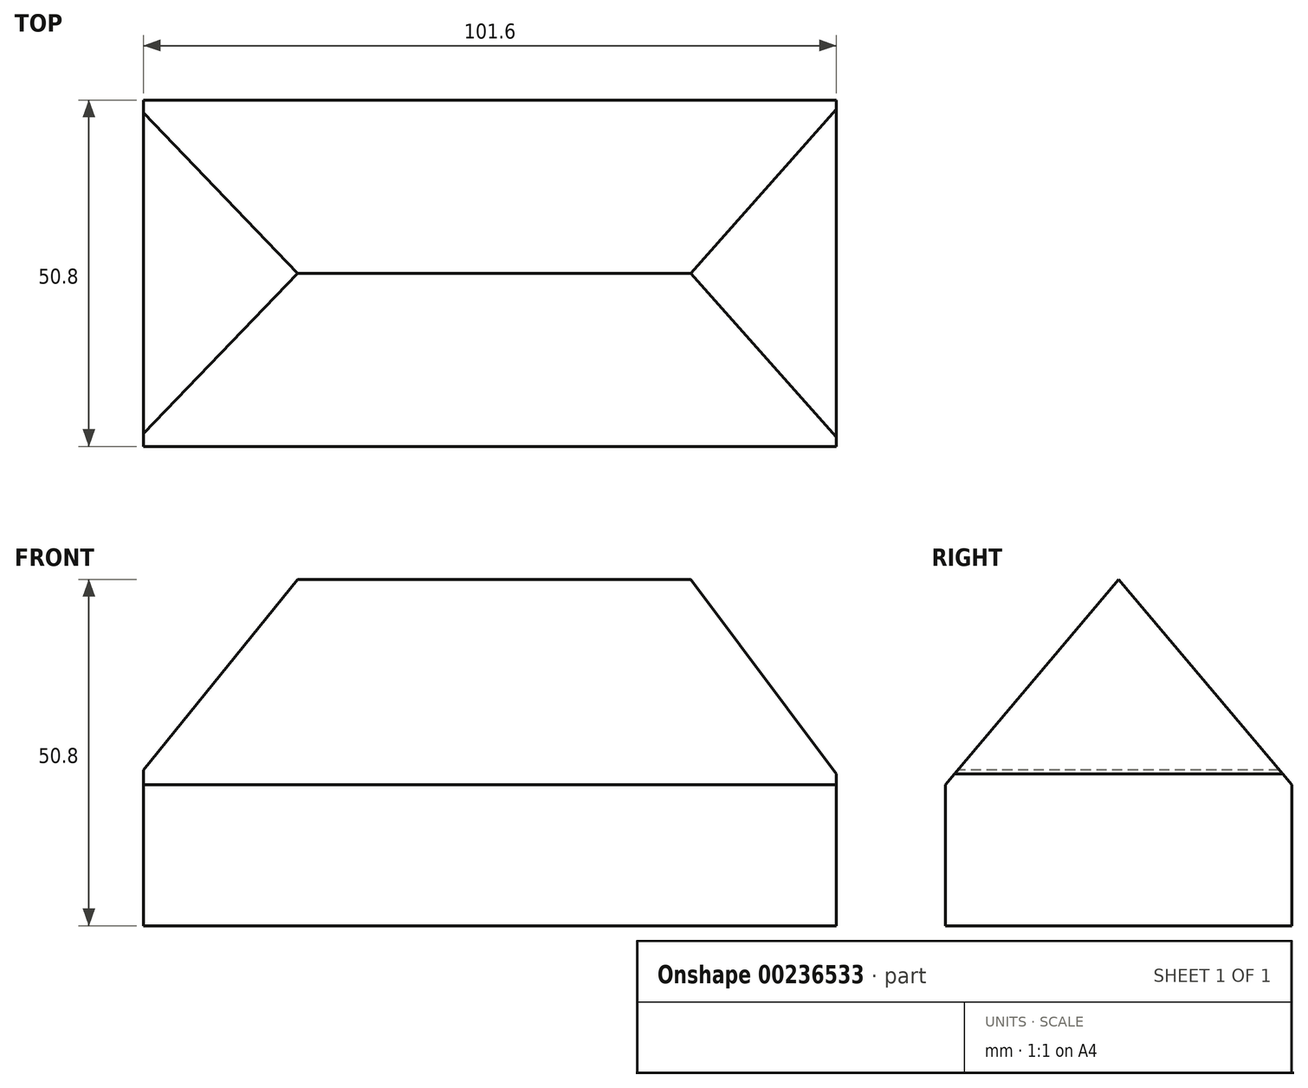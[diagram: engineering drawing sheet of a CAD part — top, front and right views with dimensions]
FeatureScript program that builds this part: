
annotation { "Feature Type Name" : "Feature", "Feature Type Description" : "" }
export const myFeature = defineFeature(function(context is Context, id is Id, definition is map)
    precondition{}
    {
        {
            var Q0;
            Q0=qCreatedBy(makeId("Top.planeOp"),FACE);
            var sketch = newSketch(context, id + "F0", { "sketchPlane" : qUnion([Q0])});
            skLineSegment(sketch, "E0.bottom", {"start": v(-44.73, 27.15) * mm, "end": v(56.87, 27.15) * mm});
            skLineSegment(sketch, "E0.top", {"start": v(-44.73, -23.65) * mm, "end": v(56.87, -23.65) * mm});
            skLineSegment(sketch, "E0.left", {"start": v(-44.73, 27.15) * mm, "end": v(-44.73, -23.65) * mm});
            skLineSegment(sketch, "E0.right", {"start": v(56.87, 27.15) * mm, "end": v(56.87, -23.65) * mm});
            skSolve(sketch);
        }
        {
            var Q0;
            Q0=makeQuery(id+"F0.imprint","IMPRINT",FACE,{"disambiguationData":[TD([[makeQuery(id+"F0.imprint","IMPRINT",EDGE,{"derivedFrom":sQuery(id+"F0.wireOp",EDGE,"E0.bottom")}),-1.0]])]});
            extrude(context, id + "F1", {"entities" : qUnion([Q0]), "depth" : 50.8 * mm});
        }
        {
            var Q0;
            Q0=makeQuery(id+"F1.opExtrude","SWEPT_FACE",FACE,{"disambiguationData":[OSD([sQuery(id+"F0.wireOp",EDGE,"E0.left")])]});
            var sketch = newSketch(context, id + "F2", { "sketchPlane" : qUnion([Q0])});
            skLineSegment(sketch, "E1", {"start": v(-1.75, 50.8) * mm, "end": v(23.65, 20.65) * mm});
            skLineSegment(sketch, "E2", {"start": v(23.65, 20.65) * mm, "end": v(23.65, 50.8) * mm});
            skLineSegment(sketch, "E3", {"start": v(23.65, 50.8) * mm, "end": v(-1.75, 50.8) * mm});
            skLineSegment(sketch, "E4", {"start": v(-27.15, 50.8) * mm, "end": v(-27.15, 20.65) * mm});
            skLineSegment(sketch, "E5", {"start": v(-27.15, 20.65) * mm, "end": v(-1.75, 50.8) * mm});
            skLineSegment(sketch, "E6", {"start": v(-27.15, 50.8) * mm, "end": v(-1.75, 50.8) * mm});
            skSolve(sketch);
        }
        {
            var Q0;
            Q0=makeQuery(id+"F2.imprint","IMPRINT",FACE,{"disambiguationData":[TD([[makeQuery(id+"F2.imprint","IMPRINT",EDGE,{"derivedFrom":sQuery(id+"F2.wireOp",EDGE,"E4")}),1.0]])]});
            var Q1;
            Q1=makeQuery(id+"F2.imprint","IMPRINT",FACE,{"disambiguationData":[TD([[makeQuery(id+"F2.imprint","IMPRINT",EDGE,{"derivedFrom":sQuery(id+"F2.wireOp",EDGE,"E1")}),1.0]])]});
            extrude(context, id + "F3", {"entities" : qUnion([Q0, Q1]), "operationType" : NewBodyOperationType.REMOVE, "oppositeDirection" : true, "depth" : 115.82 * mm});
        }
        {
            var Q0;
            Q0=qCreatedBy(makeId("Front.planeOp"),FACE);
            var sketch = newSketch(context, id + "F4", { "sketchPlane" : qUnion([Q0])});
            skLineSegment(sketch, "E7", {"start": v(35.1, 51.36) * mm, "end": v(57.3, 51.36) * mm});
            skLineSegment(sketch, "E8", {"start": v(57.3, 51.36) * mm, "end": v(57.3, 21.68) * mm});
            skLineSegment(sketch, "E9", {"start": v(57.3, 21.68) * mm, "end": v(35.1, 51.36) * mm});
            skLineSegment(sketch, "E10", {"start": v(-44.9, 51.36) * mm, "end": v(-21.68, 51.36) * mm});
            skLineSegment(sketch, "E11", {"start": v(-21.68, 51.36) * mm, "end": v(-45.68, 21.68) * mm});
            skLineSegment(sketch, "E12", {"start": v(-45.68, 21.68) * mm, "end": v(-44.9, 51.36) * mm});
            skSolve(sketch);
        }
        {
            var Q0;
            Q0=makeQuery(id+"F4.imprint","IMPRINT",FACE,{"disambiguationData":[TD([[makeQuery(id+"F4.imprint","IMPRINT",EDGE,{"derivedFrom":sQuery(id+"F4.wireOp",EDGE,"E10")}),-1.0]])]});
            var Q1;
            Q1=makeQuery(id+"F4.imprint","IMPRINT",FACE,{"disambiguationData":[TD([[makeQuery(id+"F4.imprint","IMPRINT",EDGE,{"derivedFrom":sQuery(id+"F4.wireOp",EDGE,"E7")}),-1.0]])]});
            var Q2;
            Q2=sQuery(id+"F4.wireOp",EDGE,"E10");
            var Q3;
            Q3=sQuery(id+"F4.wireOp",EDGE,"E12");
            var Q4;
            Q4=sQuery(id+"F4.wireOp",EDGE,"E11");
            extrude(context, id + "F5", {"entities" : qUnion([Q0, Q1]), "operationType" : NewBodyOperationType.REMOVE, "surfaceEntities" : qUnion([Q2, Q3, Q4]), "oppositeDirection" : true, "depth" : 33.53 * mm});
        }
        {
            var Q0;
            Q0=makeQuery(id+"F5.boolean.opBoolean","COPY",FACE,{"derivedFrom":makeQuery(id+"F5.opExtrude","CAP_FACE",FACE,{"disambiguationData":[OSD([sQuery(id+"F4.wireOp",EDGE,"E7"),sQuery(id+"F4.wireOp",EDGE,"E8"),sQuery(id+"F4.wireOp",EDGE,"E9")])],"isStart":true})});
            var Q1;
            Q1=makeQuery(id+"F5.boolean.opBoolean","COPY",FACE,{"derivedFrom":makeQuery(id+"F5.opExtrude","CAP_FACE",FACE,{"disambiguationData":[OSD([sQuery(id+"F4.wireOp",EDGE,"E10"),sQuery(id+"F4.wireOp",EDGE,"E11"),sQuery(id+"F4.wireOp",EDGE,"E12")])],"isStart":true})});
            extrude(context, id + "F6", {"entities" : qUnion([Q0, Q1]), "operationType" : NewBodyOperationType.REMOVE, "oppositeDirection" : true, "depth" : 41.4 * mm});
        }
    });
